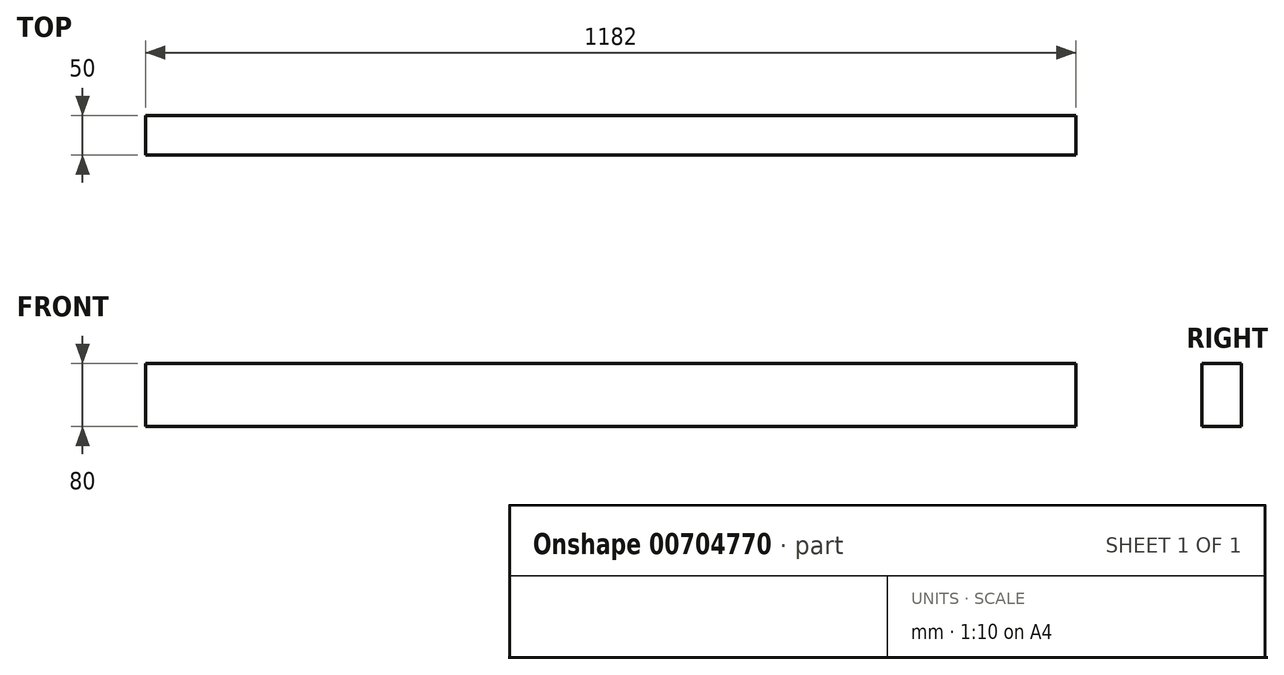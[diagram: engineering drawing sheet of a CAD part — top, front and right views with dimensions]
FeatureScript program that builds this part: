
annotation { "Feature Type Name" : "Feature", "Feature Type Description" : "" }
export const myFeature = defineFeature(function(context is Context, id is Id, definition is map)
    precondition{}
    {
        {
            var Q0;
            Q0=qCreatedBy(makeId("Front.planeOp"),FACE);
            var sketch = newSketch(context, id + "F0", { "sketchPlane" : qUnion([Q0])});
            skLineSegment(sketch, "E0.bottom", {"start": v(18.39, 0) * mm, "end": v(1200.39, 0) * mm});
            skLineSegment(sketch, "E0.top", {"start": v(18.39, 80) * mm, "end": v(1200.39, 80) * mm});
            skLineSegment(sketch, "E0.left", {"start": v(18.39, 0) * mm, "end": v(18.39, 80) * mm});
            skLineSegment(sketch, "E0.right", {"start": v(1200.39, 0) * mm, "end": v(1200.39, 80) * mm});
            skSolve(sketch);
        }
        {
            var Q0;
            Q0 = qSketchRegion(id + "F0", true);
            extrude(context, id + "F1", {"entities" : qUnion([Q0]), "depth" : 50 * mm, "offsetDistance" : 25 * mm});
        }
    });
